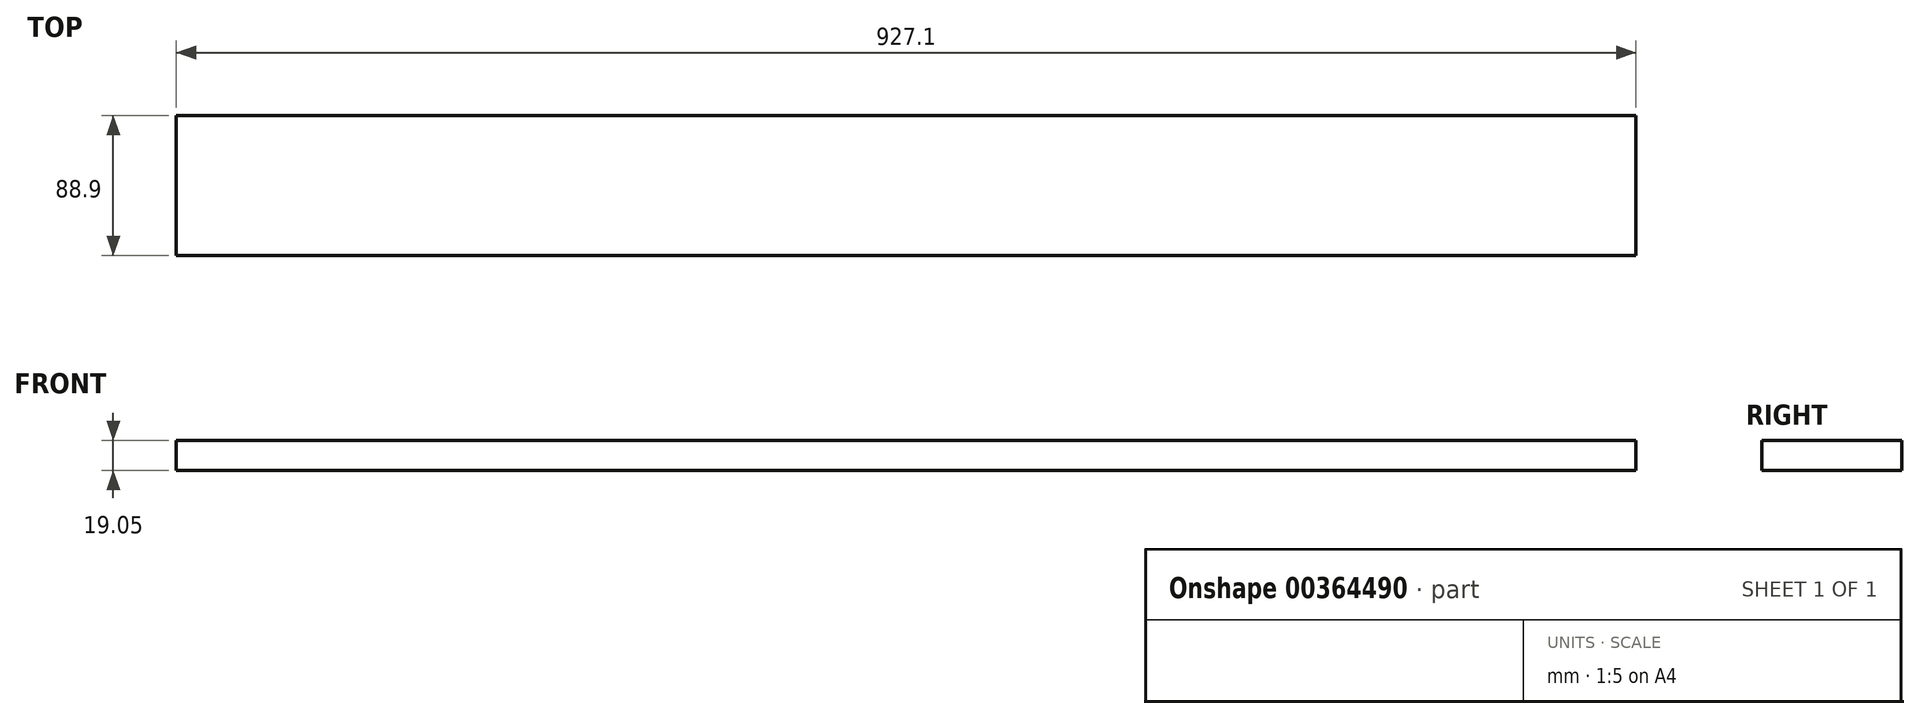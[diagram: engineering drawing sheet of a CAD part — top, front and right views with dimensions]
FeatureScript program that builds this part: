
annotation { "Feature Type Name" : "Feature", "Feature Type Description" : "" }
export const myFeature = defineFeature(function(context is Context, id is Id, definition is map)
    precondition{}
    {
        {
            var Q0;
            Q0=qCreatedBy(makeId("Top.planeOp"),FACE);
            var sketch = newSketch(context, id + "F0", { "sketchPlane" : qUnion([Q0])});
            skLineSegment(sketch, "E0.bottom", {"start": v(0, 0) * mm, "end": v(927.1, 0) * mm});
            skLineSegment(sketch, "E0.top", {"start": v(0, 88.9) * mm, "end": v(927.1, 88.9) * mm});
            skLineSegment(sketch, "E0.left", {"start": v(0, 0) * mm, "end": v(0, 88.9) * mm});
            skLineSegment(sketch, "E0.right", {"start": v(927.1, 0) * mm, "end": v(927.1, 88.9) * mm});
            skSolve(sketch);
        }
        {
            var Q0;
            Q0 = qSketchRegion(id + "F0", true);
            extrude(context, id + "F1", {"entities" : qUnion([Q0]), "depth" : 19.05 * mm});
        }
    });
